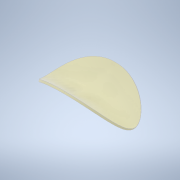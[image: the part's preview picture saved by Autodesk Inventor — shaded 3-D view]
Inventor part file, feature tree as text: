
AUTODESK INVENTOR PART (.ipt)
format: ipt  version: 2022 (Build 260153070, 153G)  size: 495,104 bytes
history: native  units: mm
features: other x6, sketch x4, plane x2, extrude x2, thicken_offset x1, surface_op x1
ambient origin geometry x8: Origin, YZ Plane, XZ Plane, XY Plane, X Axis, Y Axis, Z Axis, Center Point
bodies: Body1 (feature_tree), Body2 (feature_tree), Body3 (feature_tree), Body4 (feature_tree)
feature tree (16):
  other  "Work Axis1"
  plane  "Work Plane1"
  sketch  "Sketch3"  dims[d10=1.5875mm d11=0.1mm]
  plane  "Work Plane3"
  thicken_offset  "Thicken2"
  other  "Work Axis3"
  other  "Work Point1"
  sketch  "Sketch1"  dims[d0=45.72mm d1=0.0mm d2=10.0mm d3=0.0mm]
  other  "Srf1"
  sketch  "Sketch2"  dims[d8=5.0mm d9=0.0mm]
  other  "Srf2"
  sketch  "Sketch4"  dims[d13=19.05mm d14=75.692mm]
  other  "Srf4"
  extrude  "ExtrusionSrf1"  Depth=10.0mm TaperAngle=0.0deg
  extrude  "ExtrusionSrf2"  TaperAngle=0.0deg  [1 undecoded]
  surface_op  "Boundary Patch2"
note: 1 required parameter value undecoded (feature->parameter linkage not recoverable at this tier; creation-order binding heuristic only, values carry confidence <= 0.55)
